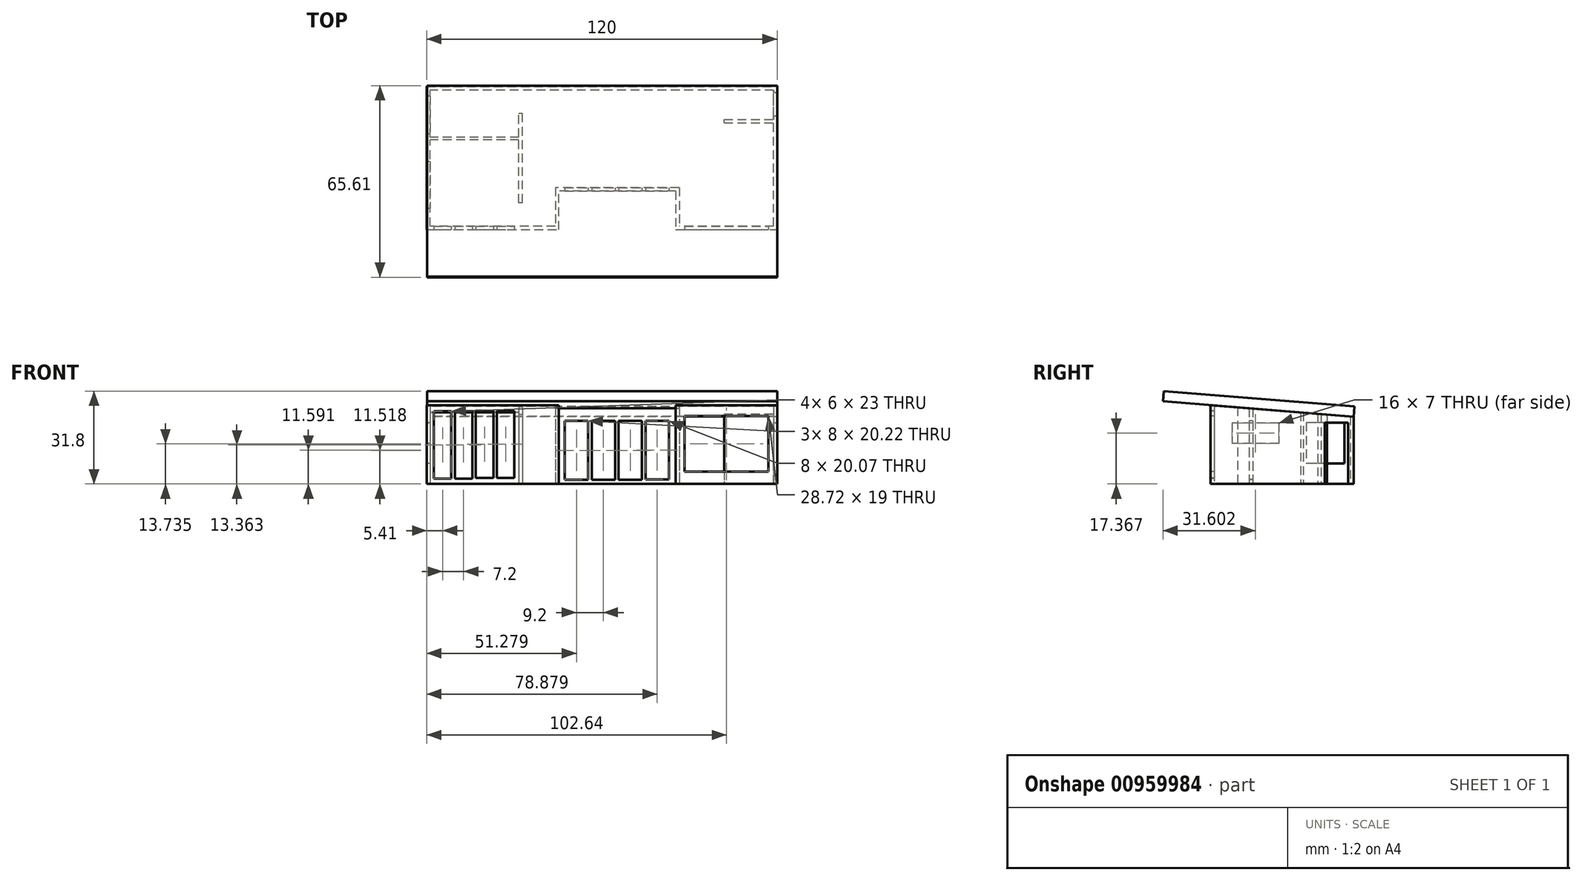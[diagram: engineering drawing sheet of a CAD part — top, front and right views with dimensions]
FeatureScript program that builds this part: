
annotation { "Feature Type Name" : "Feature", "Feature Type Description" : "" }
export const myFeature = defineFeature(function(context is Context, id is Id, definition is map)
    precondition{}
    {
        {
            var Q0;
            Q0=qCreatedBy(makeId("Top.planeOp"),FACE);
            var sketch = newSketch(context, id + "F0", { "sketchPlane" : qUnion([Q0])});
            skLineSegment(sketch, "E0.bottom", {"start": v(-76.38, 49) * mm, "end": v(43.62, 49) * mm});
            skLineSegment(sketch, "E0.top", {"start": v(-76.38, 0) * mm, "end": v(-31.1, 0) * mm});
            skLineSegment(sketch, "E0.left", {"start": v(-76.38, 49) * mm, "end": v(-76.38, 0) * mm});
            skLineSegment(sketch, "E0.right", {"start": v(43.62, 49) * mm, "end": v(43.62, 0) * mm});
            skLineSegment(sketch, "E1.bottom", {"start": v(-75.18, 47.8) * mm, "end": v(42.42, 47.8) * mm});
            skLineSegment(sketch, "E1.top", {"start": v(-75.18, 1.2) * mm, "end": v(-32.3, 1.2) * mm});
            skLineSegment(sketch, "E1.left", {"start": v(-75.18, 47.8) * mm, "end": v(-75.18, 31.66) * mm});
            skLineSegment(sketch, "E1.right", {"start": v(42.42, 47.8) * mm, "end": v(42.42, 37.8) * mm});
            skLineSegment(sketch, "E2.bottom", {"start": v(-75.18, 30.8) * mm, "end": v(-44.86, 30.8) * mm});
            skLineSegment(sketch, "E2.top", {"start": v(-75.18, 31.66) * mm, "end": v(-44.86, 31.66) * mm});
            skLineSegment(sketch, "E3.bottom", {"start": v(-44.86, 39.8) * mm, "end": v(-43.66, 39.8) * mm});
            skLineSegment(sketch, "E3.top", {"start": v(-44.86, 9.2) * mm, "end": v(-43.66, 9.2) * mm});
            skLineSegment(sketch, "E3.left", {"start": v(-44.86, 39.8) * mm, "end": v(-44.86, 31.66) * mm});
            skLineSegment(sketch, "E3.right", {"start": v(-43.66, 39.8) * mm, "end": v(-43.66, 9.2) * mm});
            skLineSegment(sketch, "E4.bottom", {"start": v(42.42, 37.8) * mm, "end": v(25.42, 37.8) * mm});
            skLineSegment(sketch, "E4.top", {"start": v(42.42, 36.6) * mm, "end": v(25.42, 36.6) * mm});
            skLineSegment(sketch, "E4.right", {"start": v(25.42, 37.8) * mm, "end": v(25.42, 36.6) * mm});
            skLineSegment(sketch, "E5.top", {"start": v(-31.1, 13.2) * mm, "end": v(8.9, 13.2) * mm});
            skLineSegment(sketch, "E5.left", {"start": v(-31.1, 1.2) * mm, "end": v(-31.1, 13.2) * mm});
            skLineSegment(sketch, "E5.right", {"start": v(8.9, 1.2) * mm, "end": v(8.9, 13.2) * mm});
            skLineSegment(sketch, "E6.top", {"start": v(-32.3, 14.4) * mm, "end": v(10.1, 14.4) * mm});
            skLineSegment(sketch, "E6.left", {"start": v(-32.3, 1.2) * mm, "end": v(-32.3, 14.4) * mm});
            skLineSegment(sketch, "E6.right", {"start": v(10.1, 1.2) * mm, "end": v(10.1, 14.4) * mm});
            skLineSegment(sketch, "E7.trimOffspring", {"start": v(-44.86, 30.8) * mm, "end": v(-44.86, 9.2) * mm});
            skLineSegment(sketch, "E8.trimOffspring", {"start": v(-75.18, 30.8) * mm, "end": v(-75.18, 1.2) * mm});
            skLineSegment(sketch, "E9.trimOffspring", {"start": v(10.1, 1.2) * mm, "end": v(42.42, 1.2) * mm});
            skLineSegment(sketch, "E10.trimOffspring", {"start": v(42.42, 36.6) * mm, "end": v(42.42, 1.2) * mm});
            skLineSegment(sketch, "E11", {"start": v(-31.1, 1.2) * mm, "end": v(-31.1, 0) * mm});
            skLineSegment(sketch, "E12", {"start": v(8.9, 1.2) * mm, "end": v(8.9, 0) * mm});
            skLineSegment(sketch, "E13.trimOffspring", {"start": v(8.9, 0) * mm, "end": v(43.62, 0) * mm});
            skSolve(sketch);
        }
        {
            var Q0;
            Q0=makeQuery(id+"F0.imprint","IMPRINT",FACE,{"disambiguationData":[TD([[makeQuery(id+"F0.imprint","IMPRINT",EDGE,{"derivedFrom":sQuery(id+"F0.wireOp",EDGE,"E0.bottom")}),-1.0]])]});
            extrude(context, id + "F1", {"entities" : qUnion([Q0]), "depth" : 27 * mm, "offsetDistance" : 25 * mm});
        }
        {
            var Q0;
            Q0=makeQuery(id+"F1.opExtrude","SWEPT_FACE",FACE,{"disambiguationData":[OSD([sQuery(id+"F0.wireOp",EDGE,"E0.top")])]});
            var sketch = newSketch(context, id + "F2", { "sketchPlane" : qUnion([Q0])});
            skLineSegment(sketch, "E14.bottom", {"start": v(-73.97, 24.86) * mm, "end": v(-67.97, 24.86) * mm});
            skLineSegment(sketch, "E14.top", {"start": v(-73.97, 1.86) * mm, "end": v(-67.97, 1.86) * mm});
            skLineSegment(sketch, "E14.left", {"start": v(-73.97, 24.86) * mm, "end": v(-73.97, 1.86) * mm});
            skLineSegment(sketch, "E14.right", {"start": v(-67.97, 24.86) * mm, "end": v(-67.97, 1.86) * mm});
            skLineSegment(sketch, "E15.bottom", {"start": v(-66.77, 24.86) * mm, "end": v(-60.77, 24.86) * mm});
            skLineSegment(sketch, "E15.top", {"start": v(-66.77, 1.86) * mm, "end": v(-60.77, 1.86) * mm});
            skLineSegment(sketch, "E15.left", {"start": v(-66.77, 24.86) * mm, "end": v(-66.77, 1.86) * mm});
            skLineSegment(sketch, "E15.right", {"start": v(-60.77, 24.86) * mm, "end": v(-60.77, 1.86) * mm});
            skLineSegment(sketch, "E16.bottom", {"start": v(-59.57, 25.1) * mm, "end": v(-53.57, 25.1) * mm});
            skLineSegment(sketch, "E16.top", {"start": v(-59.57, 2.1) * mm, "end": v(-53.57, 2.1) * mm});
            skLineSegment(sketch, "E16.left", {"start": v(-59.57, 25.1) * mm, "end": v(-59.57, 2.1) * mm});
            skLineSegment(sketch, "E16.right", {"start": v(-53.57, 25.1) * mm, "end": v(-53.57, 2.1) * mm});
            skLineSegment(sketch, "E17.bottom", {"start": v(-52.37, 25.1) * mm, "end": v(-46.37, 25.1) * mm});
            skLineSegment(sketch, "E17.top", {"start": v(-52.37, 2.1) * mm, "end": v(-46.37, 2.1) * mm});
            skLineSegment(sketch, "E17.left", {"start": v(-52.37, 25.1) * mm, "end": v(-52.37, 2.1) * mm});
            skLineSegment(sketch, "E17.right", {"start": v(-46.37, 25.1) * mm, "end": v(-46.37, 2.1) * mm});
            skSolve(sketch);
        }
        {
            var Q0;
            Q0=makeQuery(id+"F2.imprint","IMPRINT",FACE,{"disambiguationData":[TD([[makeQuery(id+"F2.imprint","IMPRINT",EDGE,{"derivedFrom":sQuery(id+"F2.wireOp",EDGE,"E14.bottom")}),-1.0]])]});
            var Q1;
            Q1=makeQuery(id+"F2.imprint","IMPRINT",FACE,{"disambiguationData":[TD([[makeQuery(id+"F2.imprint","IMPRINT",EDGE,{"derivedFrom":sQuery(id+"F2.wireOp",EDGE,"E15.bottom")}),-1.0]])]});
            var Q2;
            Q2=makeQuery(id+"F2.imprint","IMPRINT",FACE,{"disambiguationData":[TD([[makeQuery(id+"F2.imprint","IMPRINT",EDGE,{"derivedFrom":sQuery(id+"F2.wireOp",EDGE,"E16.bottom")}),-1.0]])]});
            var Q3;
            Q3=makeQuery(id+"F2.imprint","IMPRINT",FACE,{"disambiguationData":[TD([[makeQuery(id+"F2.imprint","IMPRINT",EDGE,{"derivedFrom":sQuery(id+"F2.wireOp",EDGE,"E17.bottom")}),-1.0]])]});
            extrude(context, id + "F3", {"entities" : qUnion([Q0, Q1, Q2, Q3]), "operationType" : NewBodyOperationType.REMOVE, "oppositeDirection" : true, "depth" : 1.2 * mm, "offsetDistance" : 25 * mm});
        }
        {
            var Q0;
            Q0=makeQuery(id+"F1.opExtrude","SWEPT_FACE",FACE,{"disambiguationData":[OSD([sQuery(id+"F0.wireOp",EDGE,"E0.left")])]});
            var sketch = newSketch(context, id + "F4", { "sketchPlane" : qUnion([Q0])});
            skLineSegment(sketch, "E18.bottom", {"start": v(-45.78, 21) * mm, "end": v(-32.78, 21) * mm});
            skLineSegment(sketch, "E18.top", {"start": v(-45.78, 7) * mm, "end": v(-32.78, 7) * mm});
            skLineSegment(sketch, "E18.left", {"start": v(-45.78, 21) * mm, "end": v(-45.78, 7) * mm});
            skLineSegment(sketch, "E18.right", {"start": v(-32.78, 21) * mm, "end": v(-32.78, 7) * mm});
            skLineSegment(sketch, "E19.bottom", {"start": v(-23.27, 20.87) * mm, "end": v(-7.27, 20.87) * mm});
            skLineSegment(sketch, "E19.top", {"start": v(-23.27, 13.87) * mm, "end": v(-7.27, 13.87) * mm});
            skLineSegment(sketch, "E19.left", {"start": v(-23.27, 20.87) * mm, "end": v(-23.27, 13.87) * mm});
            skLineSegment(sketch, "E19.right", {"start": v(-7.27, 20.87) * mm, "end": v(-7.27, 13.87) * mm});
            skSolve(sketch);
        }
        {
            var Q0;
            Q0=makeQuery(id+"F4.imprint","IMPRINT",FACE,{"disambiguationData":[TD([[makeQuery(id+"F4.imprint","IMPRINT",EDGE,{"derivedFrom":sQuery(id+"F4.wireOp",EDGE,"E18.bottom")}),-1.0]])]});
            var Q1;
            Q1=makeQuery(id+"F4.imprint","IMPRINT",FACE,{"disambiguationData":[TD([[makeQuery(id+"F4.imprint","IMPRINT",EDGE,{"derivedFrom":sQuery(id+"F4.wireOp",EDGE,"E19.bottom")}),-1.0]])]});
            extrude(context, id + "F5", {"entities" : qUnion([Q0, Q1]), "operationType" : NewBodyOperationType.REMOVE, "oppositeDirection" : true, "depth" : 1.2 * mm, "offsetDistance" : 25 * mm});
        }
        {
            var Q0;
            Q0=makeQuery(id+"F1.opExtrude","SWEPT_FACE",FACE,{"disambiguationData":[OSD([sQuery(id+"F0.wireOp",EDGE,"E13.trimOffspring")])]});
            var sketch = newSketch(context, id + "F6", { "sketchPlane" : qUnion([Q0])});
            skLineSegment(sketch, "E20.bottom", {"start": v(11.9, 23.23) * mm, "end": v(40.62, 23.23) * mm});
            skLineSegment(sketch, "E20.top", {"start": v(11.9, 4.23) * mm, "end": v(40.62, 4.23) * mm});
            skLineSegment(sketch, "E20.left", {"start": v(11.9, 23.23) * mm, "end": v(11.9, 4.23) * mm});
            skLineSegment(sketch, "E20.right", {"start": v(40.62, 23.23) * mm, "end": v(40.62, 4.23) * mm});
            skSolve(sketch);
        }
        {
            var Q0;
            Q0=makeQuery(id+"F6.imprint","IMPRINT",FACE,{"disambiguationData":[TD([[makeQuery(id+"F6.imprint","IMPRINT",EDGE,{"derivedFrom":sQuery(id+"F6.wireOp",EDGE,"E20.bottom")}),-1.0]])]});
            extrude(context, id + "F7", {"entities" : qUnion([Q0]), "operationType" : NewBodyOperationType.REMOVE, "oppositeDirection" : true, "depth" : 1.2 * mm, "offsetDistance" : 25 * mm});
        }
        {
            var Q0;
            Q0=makeQuery(id+"F1.opExtrude","SWEPT_FACE",FACE,{"disambiguationData":[OSD([sQuery(id+"F0.wireOp",EDGE,"E5.top")])]});
            var sketch = newSketch(context, id + "F8", { "sketchPlane" : qUnion([Q0])});
            skLineSegment(sketch, "E21.bottom", {"start": v(-29.1, 21.63) * mm, "end": v(-21.1, 21.63) * mm});
            skLineSegment(sketch, "E21.top", {"start": v(-29.1, 1.4) * mm, "end": v(-21.1, 1.4) * mm});
            skLineSegment(sketch, "E21.left", {"start": v(-29.1, 21.63) * mm, "end": v(-29.1, 1.4) * mm});
            skLineSegment(sketch, "E21.right", {"start": v(-21.1, 21.63) * mm, "end": v(-21.1, 1.4) * mm});
            skLineSegment(sketch, "E22.bottom", {"start": v(-19.9, 21.63) * mm, "end": v(-11.9, 21.63) * mm});
            skLineSegment(sketch, "E22.top", {"start": v(-19.9, 1.4) * mm, "end": v(-11.9, 1.4) * mm});
            skLineSegment(sketch, "E22.left", {"start": v(-19.9, 21.63) * mm, "end": v(-19.9, 1.4) * mm});
            skLineSegment(sketch, "E22.right", {"start": v(-11.9, 21.63) * mm, "end": v(-11.9, 1.4) * mm});
            skLineSegment(sketch, "E23.bottom", {"start": v(-1.5, 21.63) * mm, "end": v(6.5, 21.63) * mm});
            skLineSegment(sketch, "E23.top", {"start": v(-1.5, 1.55) * mm, "end": v(6.5, 1.55) * mm});
            skLineSegment(sketch, "E23.left", {"start": v(-1.5, 21.63) * mm, "end": v(-1.5, 1.55) * mm});
            skLineSegment(sketch, "E23.right", {"start": v(6.5, 21.63) * mm, "end": v(6.5, 1.55) * mm});
            skLineSegment(sketch, "E24.bottom", {"start": v(-10.7, 21.63) * mm, "end": v(-2.7, 21.63) * mm});
            skLineSegment(sketch, "E24.top", {"start": v(-10.7, 1.4) * mm, "end": v(-2.7, 1.4) * mm});
            skLineSegment(sketch, "E24.left", {"start": v(-10.7, 21.63) * mm, "end": v(-10.7, 1.4) * mm});
            skLineSegment(sketch, "E24.right", {"start": v(-2.7, 21.63) * mm, "end": v(-2.7, 1.4) * mm});
            skSolve(sketch);
        }
        {
            var Q0;
            Q0=makeQuery(id+"F8.imprint","IMPRINT",FACE,{"disambiguationData":[TD([[makeQuery(id+"F8.imprint","IMPRINT",EDGE,{"derivedFrom":sQuery(id+"F8.wireOp",EDGE,"E21.bottom")}),-1.0]])]});
            var Q1;
            Q1=makeQuery(id+"F8.imprint","IMPRINT",FACE,{"disambiguationData":[TD([[makeQuery(id+"F8.imprint","IMPRINT",EDGE,{"derivedFrom":sQuery(id+"F8.wireOp",EDGE,"E22.bottom")}),-1.0]])]});
            var Q2;
            Q2=makeQuery(id+"F8.imprint","IMPRINT",FACE,{"disambiguationData":[TD([[makeQuery(id+"F8.imprint","IMPRINT",EDGE,{"derivedFrom":sQuery(id+"F8.wireOp",EDGE,"E24.bottom")}),-1.0]])]});
            var Q3;
            Q3=makeQuery(id+"F8.imprint","IMPRINT",FACE,{"disambiguationData":[TD([[makeQuery(id+"F8.imprint","IMPRINT",EDGE,{"derivedFrom":sQuery(id+"F8.wireOp",EDGE,"E23.bottom")}),-1.0]])]});
            extrude(context, id + "F9", {"entities" : qUnion([Q0, Q1, Q2, Q3]), "operationType" : NewBodyOperationType.REMOVE, "oppositeDirection" : true, "depth" : 1.2 * mm, "offsetDistance" : 25 * mm});
        }
        {
            var Q0;
            Q0=makeQuery(id+"F1.opExtrude","SWEPT_FACE",FACE,{"disambiguationData":[OSD([sQuery(id+"F0.wireOp",EDGE,"E0.right")])]});
            var sketch = newSketch(context, id + "F10", { "sketchPlane" : qUnion([Q0])});
            skLineSegment(sketch, "E25.bottom", {"start": v(39, 0) * mm, "end": v(47, 0) * mm});
            skLineSegment(sketch, "E25.top", {"start": v(39, 21) * mm, "end": v(47, 21) * mm});
            skLineSegment(sketch, "E25.left", {"start": v(39, 0) * mm, "end": v(39, 21) * mm});
            skLineSegment(sketch, "E25.right", {"start": v(47, 0) * mm, "end": v(47, 21) * mm});
            skSolve(sketch);
        }
        {
            var Q0;
            Q0=makeQuery(id+"F10.imprint","IMPRINT",FACE,{"disambiguationData":[TD([[makeQuery(id+"F10.imprint","IMPRINT",EDGE,{"derivedFrom":sQuery(id+"F10.wireOp",EDGE,"E25.bottom")}),-1.0]])]});
            extrude(context, id + "F11", {"entities" : qUnion([Q0]), "operationType" : NewBodyOperationType.REMOVE, "oppositeDirection" : true, "depth" : 1.2 * mm, "offsetDistance" : 25 * mm});
        }
        {
            var Q0;
            Q0=makeQuery(id+"F1.opExtrude","SWEPT_FACE",FACE,{"disambiguationData":[OSD([sQuery(id+"F0.wireOp",EDGE,"E0.left")])]});
            var sketch = newSketch(context, id + "F12", { "sketchPlane" : qUnion([Q0])});
            skLineSegment(sketch, "E26", {"start": v(-49, 23.06) * mm, "end": v(0, 27) * mm});
            skLineSegment(sketch, "E27", {"start": v(-49, 23.06) * mm, "end": v(-49, 27) * mm});
            skLineSegment(sketch, "E28", {"start": v(-49, 27) * mm, "end": v(0, 27) * mm});
            skSolve(sketch);
        }
        {
            var Q0;
            Q0=makeQuery(id+"F12.imprint","IMPRINT",FACE,{"disambiguationData":[TD([[makeQuery(id+"F12.imprint","IMPRINT",EDGE,{"derivedFrom":sQuery(id+"F12.wireOp",EDGE,"E26")}),1.0]])]});
            extrude(context, id + "F13", {"entities" : qUnion([Q0]), "operationType" : NewBodyOperationType.REMOVE, "endBound" : BoundingType.THROUGH_ALL, "oppositeDirection" : true, "depth" : 25 * mm, "offsetDistance" : 25 * mm});
        }
        {
            var Q0;
            Q0=makeQuery(id+"F13.boolean.opBoolean","COPY",FACE,{"derivedFrom":makeQuery(id+"F13.opExtrude","SWEPT_FACE",FACE,{"disambiguationData":[OSD([sQuery(id+"F12.wireOp",EDGE,"E26")])]})});
            var sketch = newSketch(context, id + "F14", { "sketchPlane" : qUnion([Q0])});
            skLineSegment(sketch, "E29.bottom", {"start": v(43.62, 47) * mm, "end": v(-76.28, 47) * mm});
            skLineSegment(sketch, "E29.top", {"start": v(43.62, -18.55) * mm, "end": v(-76.28, -18.55) * mm});
            skLineSegment(sketch, "E29.left", {"start": v(43.62, 47) * mm, "end": v(43.62, -18.55) * mm});
            skLineSegment(sketch, "E29.right", {"start": v(-76.28, 47) * mm, "end": v(-76.28, -18.55) * mm});
            skSolve(sketch);
        }
        {
            var Q0;
            Q0 = qSketchRegion(id + "F14", true);
            extrude(context, id + "F15", {"entities" : qUnion([Q0]), "depth" : 3.5 * mm, "offsetDistance" : 25 * mm});
        }
    });
